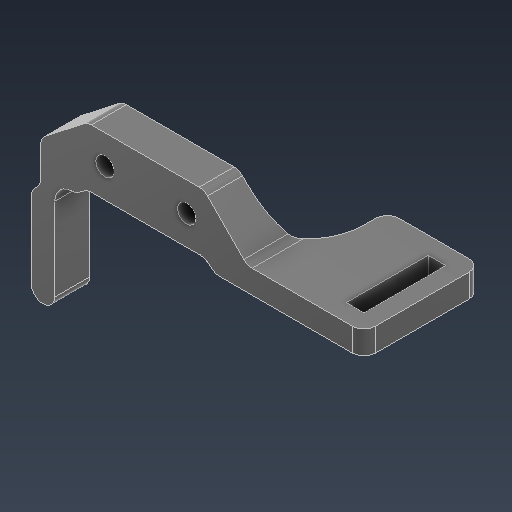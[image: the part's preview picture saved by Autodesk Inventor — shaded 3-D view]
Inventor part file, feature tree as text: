
AUTODESK INVENTOR PART (.ipt)
format: ipt  version: 2021 (Build 250183000, 183)  size: 181,248 bytes
history: native  units: mm
features: other x5, plane x1
ambient origin geometry x8: Origin, YZ Plane, XZ Plane, XY Plane, X Axis, Y Axis, Z Axis, Center Point
bodies: Solid1 (feature_tree)
feature tree (6):
  other  "mount_battery.ipt"
  other  "Solid1::mount_battery.ipt"
  other  "TaggingFeature1"
  other  "mount_sketch"
  other  "nuts_sketch"
  plane  "Work Plane1"
